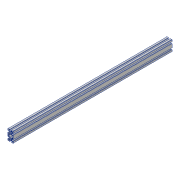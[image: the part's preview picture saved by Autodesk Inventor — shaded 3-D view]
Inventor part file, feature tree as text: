
AUTODESK INVENTOR PART (.ipt)
format: ipt  version: 2018 (Build 220112000, 112)  size: 241,664 bytes
history: native  units: mm
features: extrude x1, sketch x1
ambient origin geometry x8: Origin, YZ Plane, XZ Plane, XY Plane, X Axis, Y Axis, Z Axis, Center Point
bodies: Solid1 (feature_tree)
feature tree (2):
  extrude  "Extrusion1"  [1 undecoded]
  sketch  "Sketch1"  dims[d0=600.0mm d1=0.0mm]
note: 1 required parameter value undecoded (feature->parameter linkage not recoverable at this tier; creation-order binding heuristic only, values carry confidence <= 0.55)
